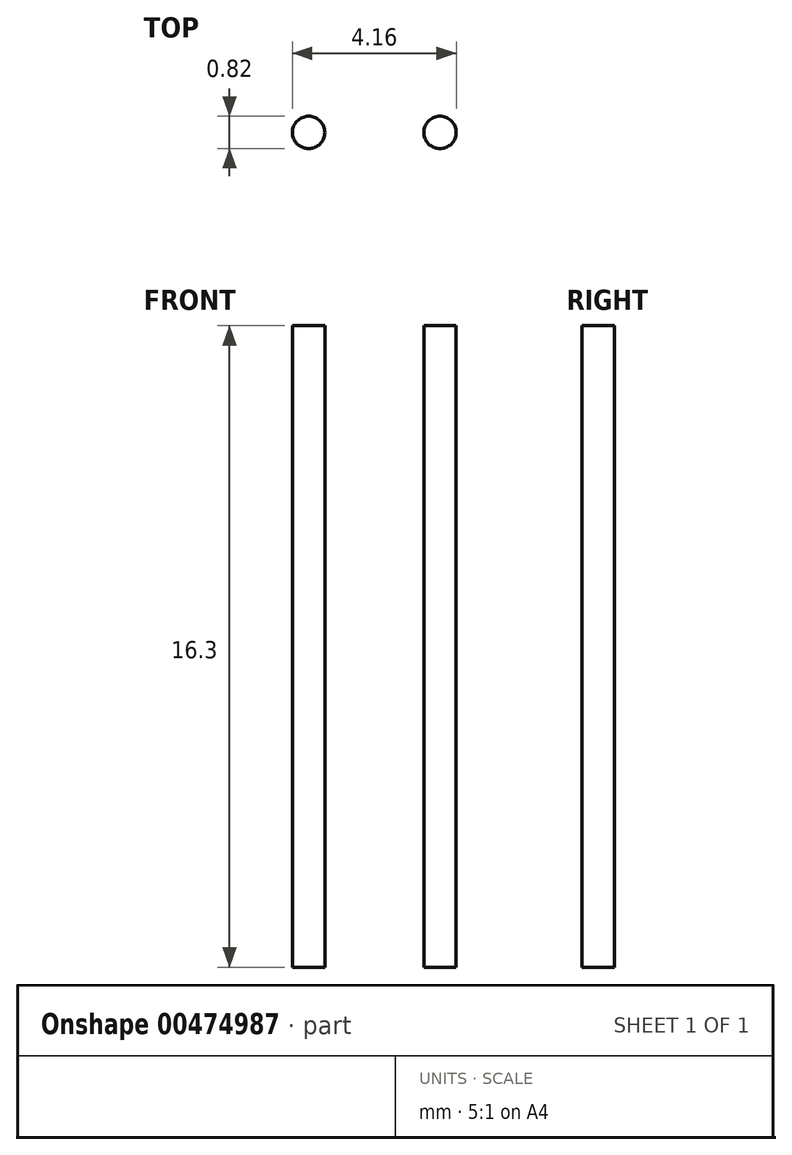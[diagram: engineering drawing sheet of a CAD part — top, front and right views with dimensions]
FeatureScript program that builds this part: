
annotation { "Feature Type Name" : "Feature", "Feature Type Description" : "" }
export const myFeature = defineFeature(function(context is Context, id is Id, definition is map)
    precondition{}
    {
        {
            var Q0;
            Q0=qCreatedBy(makeId("Top.planeOp"),FACE);
            var sketch = newSketch(context, id + "F0", { "sketchPlane" : qUnion([Q0])});
            skCircle(sketch, "E0", {"center": v(6.99, 0) * mm, "radius": 0.41 * mm});
            skCircle(sketch, "E1", {"center": v(10.33, 0) * mm, "radius": 0.41 * mm});
            skSolve(sketch);
        }
        {
            var Q0;
            Q0 = qSketchRegion(id + "F0", true);
            extrude(context, id + "F1", {"entities" : qUnion([Q0]), "depth" : 16.3 * mm});
        }
    });
